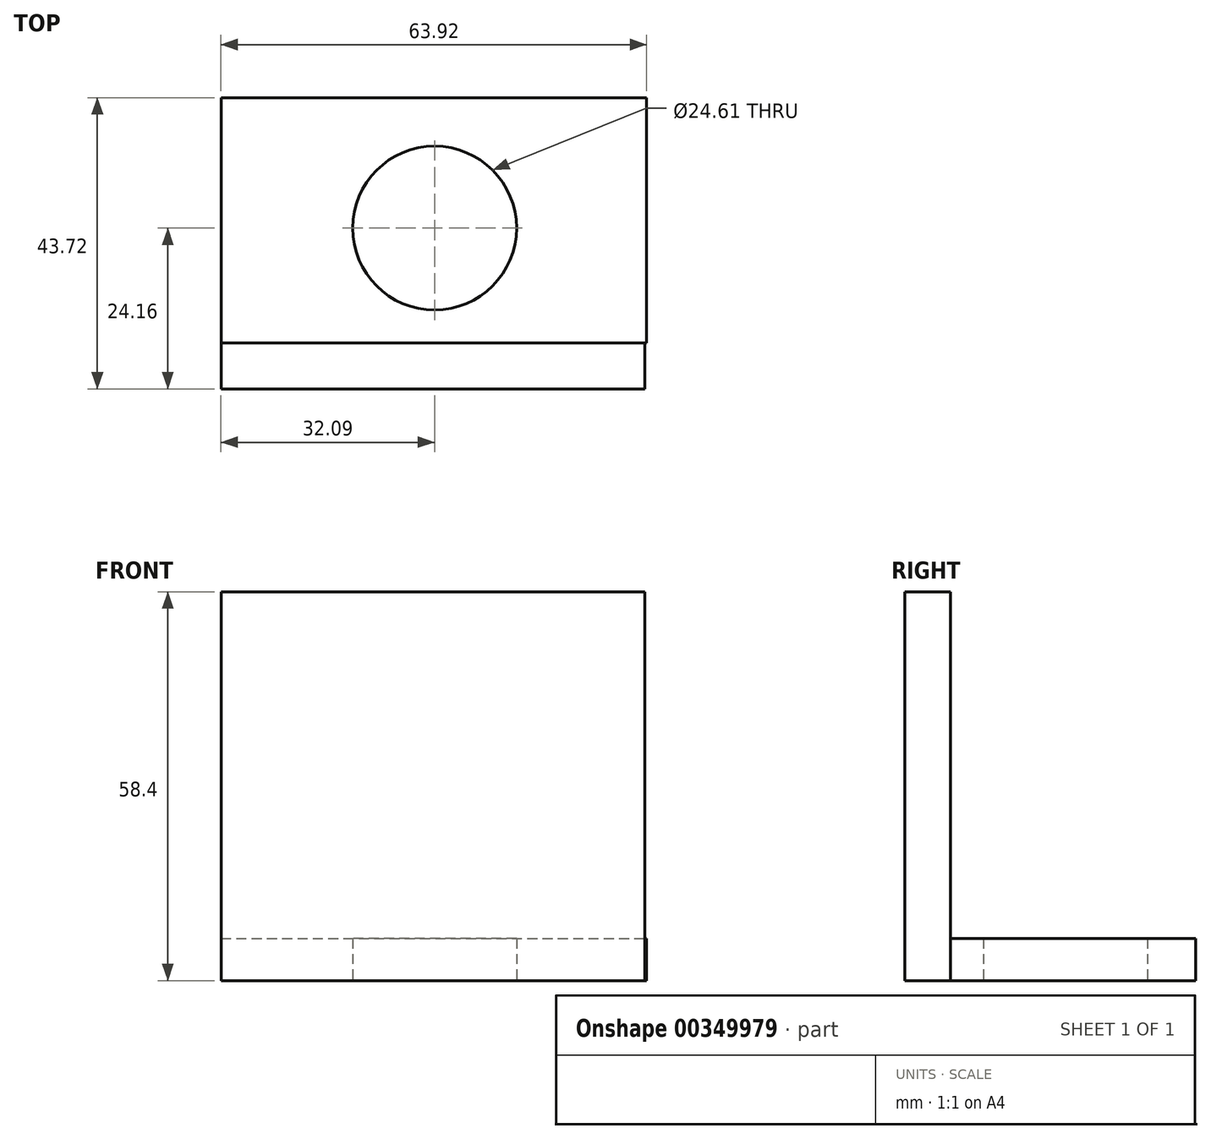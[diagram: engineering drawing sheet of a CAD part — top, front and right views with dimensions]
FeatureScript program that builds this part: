
annotation { "Feature Type Name" : "Feature", "Feature Type Description" : "" }
export const myFeature = defineFeature(function(context is Context, id is Id, definition is map)
    precondition{}
    {
        {
            var Q0;
            Q0=qCreatedBy(makeId("Top.planeOp"),FACE);
            var sketch = newSketch(context, id + "F0", { "sketchPlane" : qUnion([Q0])});
            skLineSegment(sketch, "E0.bottom", {"start": v(-32.09, 19.56) * mm, "end": v(31.83, 19.56) * mm});
            skLineSegment(sketch, "E0.top", {"start": v(-32.09, -17.26) * mm, "end": v(31.83, -17.26) * mm});
            skLineSegment(sketch, "E0.left", {"start": v(-32.09, 19.56) * mm, "end": v(-32.09, -17.26) * mm});
            skLineSegment(sketch, "E0.right", {"start": v(31.83, 19.56) * mm, "end": v(31.83, -17.26) * mm});
            skCircle(sketch, "E1", {"center": v(0, 0) * mm, "radius": 12.3 * mm});
            skSolve(sketch);
        }
        {
            var Q0;
            Q0 = qSketchRegion(id + "F0", true);
            extrude(context, id + "F1", {"entities" : qUnion([Q0]), "depth" : 6.3 * mm, "offsetDistance" : 25 * mm});
        }
        {
            var Q0;
            Q0=makeQuery(id+"F1.opExtrude","CAP_FACE",FACE,{"disambiguationData":[OSD([sQuery(id+"F0.wireOp",EDGE,"E0.bottom"),sQuery(id+"F0.wireOp",EDGE,"E0.top"),sQuery(id+"F0.wireOp",EDGE,"E0.left"),sQuery(id+"F0.wireOp",EDGE,"E0.right"),sQuery(id+"F0.wireOp",EDGE,"E1")])],"isStart":true});
            var sketch = newSketch(context, id + "F2", { "sketchPlane" : qUnion([Q0])});
            skLineSegment(sketch, "E2.bottom", {"start": v(-32.09, 17.26) * mm, "end": v(31.58, 17.26) * mm});
            skLineSegment(sketch, "E2.top", {"start": v(-32.09, 24.16) * mm, "end": v(31.58, 24.16) * mm});
            skLineSegment(sketch, "E2.left", {"start": v(-32.09, 17.26) * mm, "end": v(-32.09, 24.16) * mm});
            skLineSegment(sketch, "E2.right", {"start": v(31.58, 17.26) * mm, "end": v(31.58, 24.16) * mm});
            skSolve(sketch);
        }
        {
            var Q0;
            Q0 = qSketchRegion(id + "F2", true);
            extrude(context, id + "F3", {"entities" : qUnion([Q0]), "operationType" : NewBodyOperationType.ADD, "oppositeDirection" : true, "depth" : 58.4 * mm, "offsetDistance" : 25 * mm});
        }
    });
